# Revit family: Boiler-Weil-McLain-LGB14_20
name_source: partatom
category: Mechanical Equipment
units: mm (PartAtom-declared; Revit-internal decimal feet)

## family parameters
Always vertical = Yes
Cut with Voids When Loaded = No
OmniClass Number = 23.75.10.11.14.11
OmniClass Title = Cast-Iron Boilers
Part Type = Normal
Room Calculation Point = No
Round Connector Dimension = Use Radius
Shared = No
Work Plane-Based = No

## types (8) — shared parameters
Apparent Load = 0 VA
Casing = Metal - Weil-McLain - Paint Grey
Description = LGB Commercial Gas Boiler
Frequency = 60 Hz
Gas Connection Radius = 1"
Gas Connection Size = 2"
Height = 4' - 2 3/8"
Length = 3' - 10 1/2"
Manufacturer = Weil-McLain
Middle Panel = 0' - 5 1/2"
Number of Poles = 1
Optional WFFP Control Panel = No
Phase = 1
Power Factor = 1
Product Documentation Link = http://www.weil-mclain.com
Product Name = LGB
Product Page URL = http://www.weil-mclain.com
Radius 1 = 0' - 7"
Radius 2 = 0' - 7"
Return = 5"
Steam Return Radius = 3"
Steam Supply Radius = 3"
Supply = 6"
URL = http://www.weil-mclain.com
Voltage = 120 V

## per-type parameters (varying)
| type | Boiler Horsepower | Distance Between Vents | Gas Net IBR | Gross IBR | Left Draft Hood Outlet | Left Draft Hood Outlet Radius | Model | Net IBR | Right Draft Hood Outlet | Right Draft Hood Outlet Radius | Unit Length | Width |
| LGB-14 - Water Boiler | 40.9 | 2' - 8 1/2" | 1690000.0 Btu/h | 1369000.0 Btu/h | 12" | 6" | LGB-14 | 1190000.0 Btu/h | 14" | 7" | 2' - 11 1/2" | 5' - 11" |
| LGB-16 - Water Boiler | 47.2 | 3' - 1 1/2" | 1950000.0 Btu/h | 1580000.0 Btu/h | 14" | 7" | LGB-16 | 1373000.0 Btu/h | 14" | 7" | 3' - 4 1/2" | 6' - 9" |
| LGB-18 - Water Boiler | 53.5 | 3' - 6" | 2210000.0 Btu/h | 1790000.0 Btu/h | 16" | 8" | LGB-18 | 1557000.0 Btu/h | 16" | 8" | 3' - 9 1/2" | 7' - 7" |
| LGB-20 - Water Boiler | 59.8 | 3' - 11 1/2" | 2470000.0 Btu/h | 2001000.0 Btu/h | 16" | 8" | LGB-20 | 1740000.0 Btu/h | 16" | 8" | 4' - 2 1/2" | 8' - 5" |
| LGB-14 - Steam Boiler | 40.9 | 2' - 8 1/2" | 1690000.0 Btu/h | 1369000.0 Btu/h | 12" | 6" | LGB-14 | 1190000.0 Btu/h | 14" | 7" | 2' - 11 1/2" | 5' - 11" |
| LGB-16 - Steam Boiler | 47.2 | 3' - 1 1/2" | 1950000.0 Btu/h | 1580000.0 Btu/h | 14" | 7" | LGB-16 | 1373000.0 Btu/h | 14" | 7" | 3' - 4 1/2" | 6' - 9" |
| LGB-18 - Steam Boiler | 53.5 | 3' - 6" | 2210000.0 Btu/h | 1790000.0 Btu/h | 14" | 7" | LGB-18 | 1557000.0 Btu/h | 16" | 8" | 3' - 9 1/2" | 7' - 7" |
| LGB-20 - Steam Boiler | 59.8 | 3' - 11 1/2" | 2470000.0 Btu/h | 2001000.0 Btu/h | 16" | 8" | LGB-20 | 1740000.0 Btu/h | 16" | 8" | 4' - 2 1/2" | 8' - 5" |

## geometry (parser evidence)
native form markers: Blend x15, Sweep x6
no freeform markers — native parametric forms only
